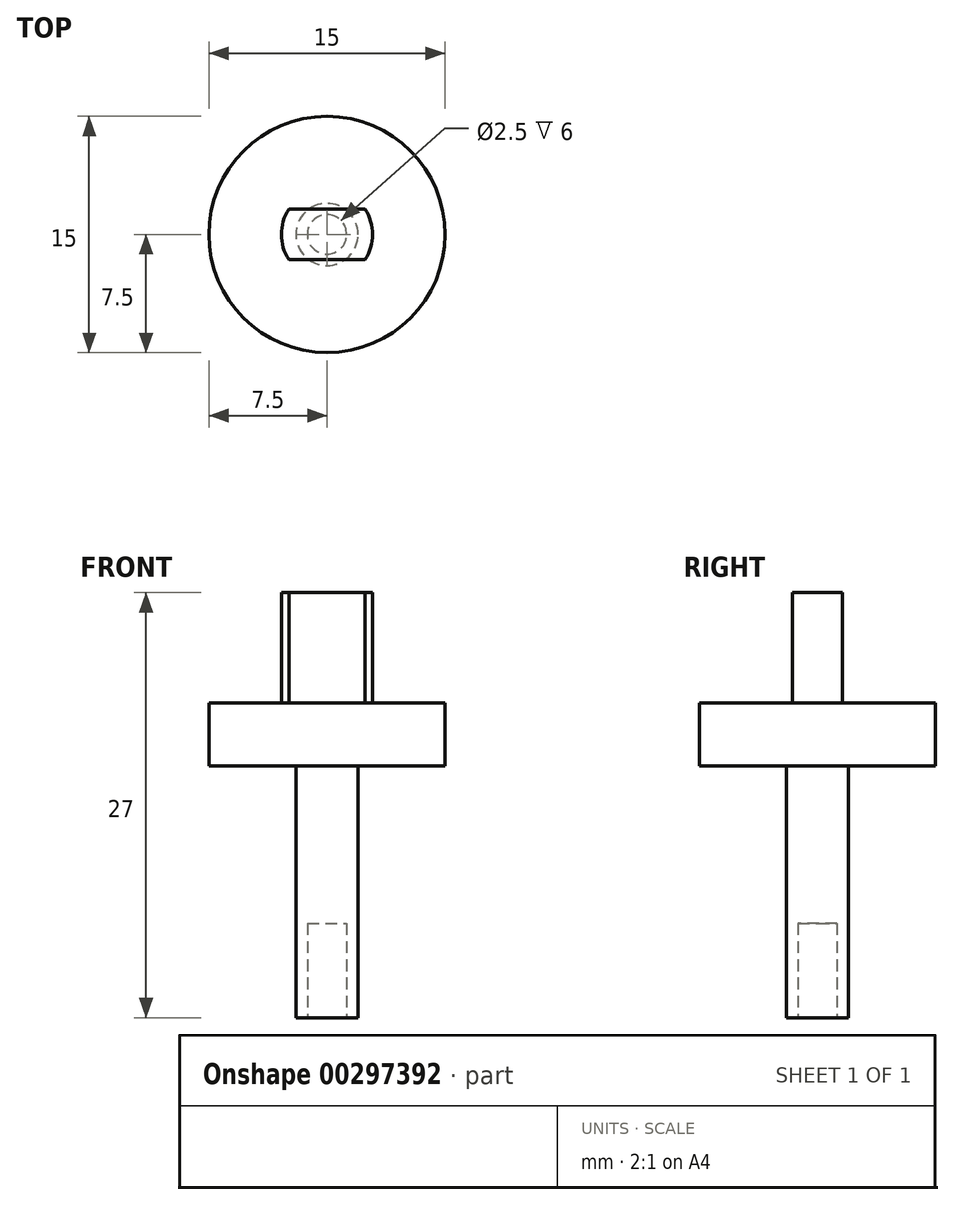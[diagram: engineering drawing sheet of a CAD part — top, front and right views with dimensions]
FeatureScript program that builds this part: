
annotation { "Feature Type Name" : "Feature", "Feature Type Description" : "" }
export const myFeature = defineFeature(function(context is Context, id is Id, definition is map)
    precondition{}
    {
        {
            var Q0;
            Q0=qCreatedBy(makeId("Top.planeOp"),FACE);
            var sketch = newSketch(context, id + "F0", { "sketchPlane" : qUnion([Q0])});
            skPoint(sketch, "E0.middle", {"position": v(0, 0) * mm});
            skArc(sketch, "E1", {"start": v(2.42, 1.6) * mm, "mid": v(2.9, 0) * mm, "end": v(2.42, -1.6) * mm});
            skArc(sketch, "E2", {"start": v(-2.42, 1.6) * mm, "mid": v(-2.9, 0) * mm, "end": v(-2.42, -1.6) * mm});
            skLineSegment(sketch, "E3", {"start": v(-2.42, 1.6) * mm, "end": v(2.42, 1.6) * mm});
            skLineSegment(sketch, "E4", {"start": v(2.42, -1.6) * mm, "end": v(-2.42, -1.6) * mm});
            skSolve(sketch);
        }
        {
            var Q0;
            Q0 = qSketchRegion(id + "F0", true);
            extrude(context, id + "F1", {"entities" : qUnion([Q0]), "depth" : 7 * mm});
        }
        {
            var Q0;
            Q0=makeQuery(id+"F1.opExtrude","CAP_FACE",FACE,{"disambiguationData":[OSD([sQuery(id+"F0.wireOp",EDGE,"E1"),sQuery(id+"F0.wireOp",EDGE,"E2"),sQuery(id+"F0.wireOp",EDGE,"E3"),sQuery(id+"F0.wireOp",EDGE,"E4")])],"isStart":true});
            var sketch = newSketch(context, id + "F2", { "sketchPlane" : qUnion([Q0])});
            skCircle(sketch, "E5", {"center": v(0, 0) * mm, "radius": 7.5 * mm});
            skSolve(sketch);
        }
        {
            var Q0;
            Q0 = qSketchRegion(id + "F2", true);
            extrude(context, id + "F3", {"entities" : qUnion([Q0]), "operationType" : NewBodyOperationType.ADD, "depth" : 4 * mm});
        }
        {
            var Q0;
            Q0=makeQuery(id+"F3.opExtrude","CAP_FACE",FACE,{"disambiguationData":[OSD([sQuery(id+"F2.wireOp",EDGE,"E5")])],"isStart":false});
            var sketch = newSketch(context, id + "F4", { "sketchPlane" : qUnion([Q0])});
            skCircle(sketch, "E6", {"center": v(0, 0) * mm, "radius": 1.98 * mm});
            skSolve(sketch);
        }
        {
            var Q0;
            Q0 = qSketchRegion(id + "F4", true);
            extrude(context, id + "F5", {"entities" : qUnion([Q0]), "operationType" : NewBodyOperationType.ADD, "depth" : 16 * mm});
        }
        {
            var Q0;
            Q0=makeQuery(id+"F5.opExtrude","CAP_FACE",FACE,{"disambiguationData":[OSD([sQuery(id+"F4.wireOp",EDGE,"E6")])],"isStart":false});
            var sketch = newSketch(context, id + "F6", { "sketchPlane" : qUnion([Q0])});
            skCircle(sketch, "E7", {"center": v(0, 0) * mm, "radius": 1.25 * mm});
            skSolve(sketch);
        }
        {
            var Q0;
            Q0 = qSketchRegion(id + "F6", true);
            extrude(context, id + "F7", {"entities" : qUnion([Q0]), "operationType" : NewBodyOperationType.REMOVE, "oppositeDirection" : true, "depth" : 6 * mm});
        }
    });
